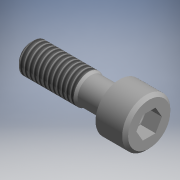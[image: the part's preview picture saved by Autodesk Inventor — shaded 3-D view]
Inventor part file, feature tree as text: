
AUTODESK INVENTOR PART (.ipt)
format: ipt  version: 2017.3 (Build 213256000, 256)  size: 138,752 bytes
history: native  units: mm (DEFAULTED — no unit token found)
features: other x28, sketch x3, revolve x2, thread x1, extrude x1
ambient origin geometry x8: Origin, YZ Plane, XZ Plane, XY Plane, X Axis, Y Axis, Z Axis, Center Point
bodies: Solid1 (feature_tree)
feature tree (35):
  revolve  "Revolution1"  [1 undecoded]
  thread  "Thread1"  [1 undecoded]
  revolve  "Revolution2"  [1 undecoded]
  extrude  "Extrusion1"  [1 undecoded]
  other  "bolt_to_plane_washer_XY"
  other  "bolt_to_plane_washer_YZ"
  other  "bolt_to_plane_washer_ZX"
  other  "bolt_to_plane_washer_X"
  other  "bolt_to_plane_washer_Y"
  other  "bolt_to_plane_washer_Z"
  other  "bolt_to_plane_washer_Center"
  other  "bolt_to_spring_washer_XY"
  other  "bolt_to_spring_washer_YZ"
  other  "bolt_to_spring_washer_ZX"
  other  "bolt_to_spring_washer_X"
  other  "bolt_to_spring_washer_Y"
  other  "bolt_to_spring_washer_Z"
  other  "bolt_to_spring_washer_Center"
  other  "screw_to_body_XY"
  other  "screw_to_body_YZ"
  other  "screw_to_body_ZX"
  other  "screw_to_body_X"
  other  "screw_to_body_Y"
  other  "screw_to_body_Z"
  other  "screw_to_body_Center"
  other  "to_washer_XY"
  other  "to_washer_YZ"
  other  "to_washer_ZX"
  other  "to_washer_X"
  other  "to_washer_Y"
  other  "to_washer_Z"
  other  "to_washer_Center"
  sketch  "Sketch_6"
  sketch  "Sketch_1"  dims[d0=360.0deg d1=14.833mm d2=0.0mm d3=360.0deg]
  sketch  "Sketch_2"  dims[d4=4.0mm d5=0.0mm d6=0.0mm d7=0.0mm]
note: 4 required parameter values undecoded (feature->parameter linkage not recoverable at this tier; creation-order binding heuristic only, values carry confidence <= 0.55)